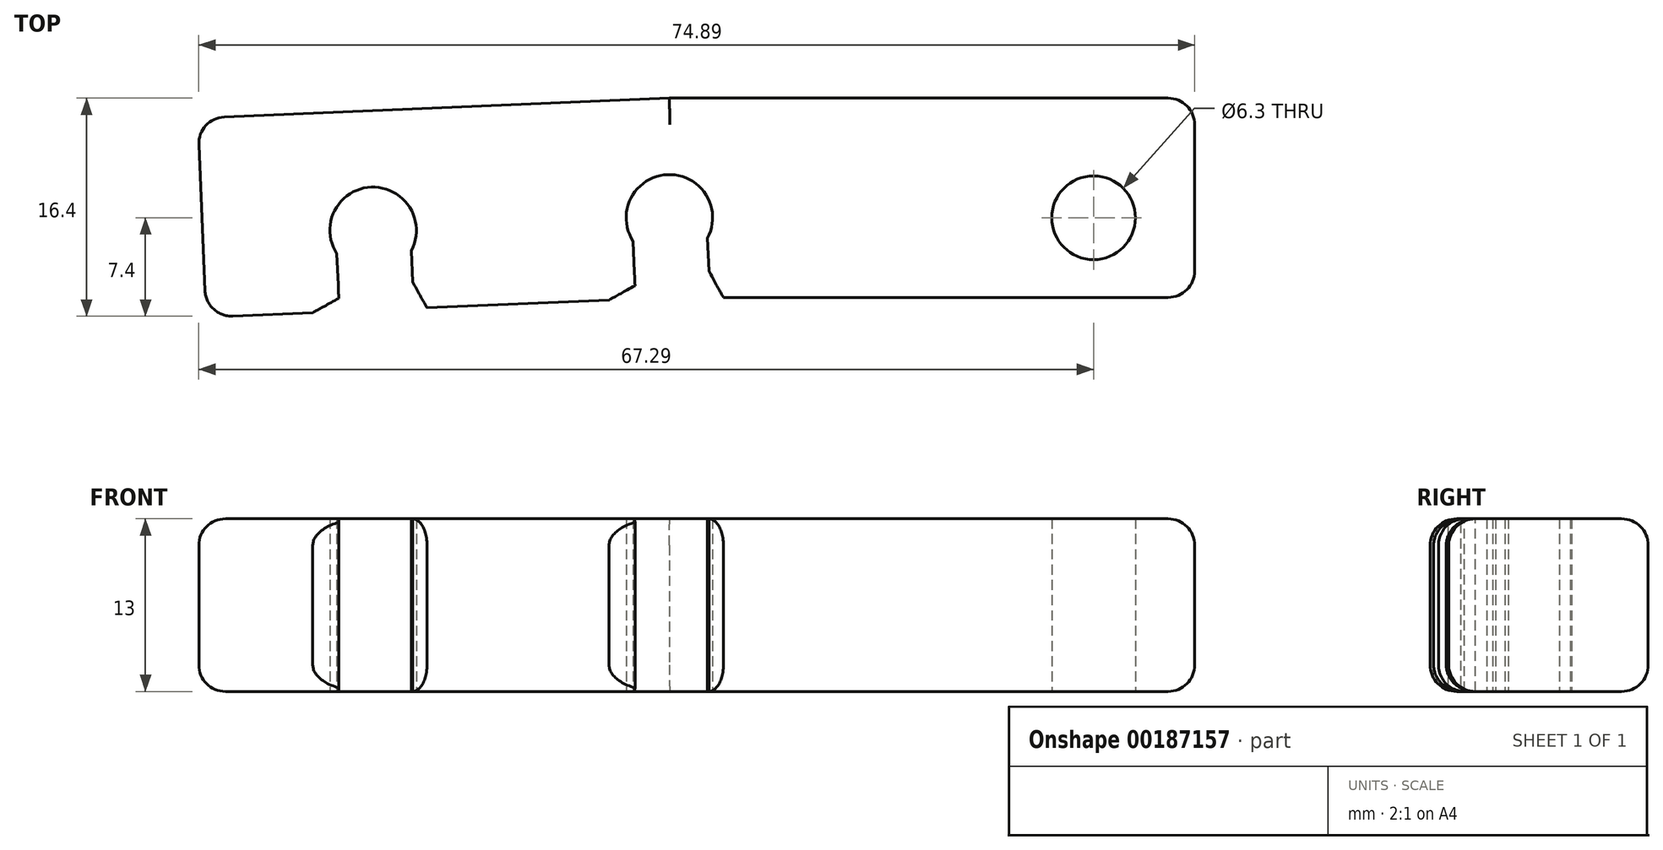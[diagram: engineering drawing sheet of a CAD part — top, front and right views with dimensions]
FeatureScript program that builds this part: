
annotation { "Feature Type Name" : "Feature", "Feature Type Description" : "" }
export const myFeature = defineFeature(function(context is Context, id is Id, definition is map)
    precondition{}
    {
        {
            var Q0;
            Q0=qCreatedBy(makeId("Top.planeOp"),FACE);
            var sketch = newSketch(context, id + "F0", { "sketchPlane" : qUnion([Q0])});
            skCircle(sketch, "E0", {"center": v(0, 0) * mm, "radius": 3.25 * mm});
            skLineSegment(sketch, "E1.bottom", {"start": v(0, 9) * mm, "end": v(39.5, 9) * mm});
            skLineSegment(sketch, "E1.top", {"start": v(0, -6) * mm, "end": v(39.5, -6) * mm});
            skLineSegment(sketch, "E1.left", {"start": v(0, 9) * mm, "end": v(0, -6) * mm});
            skLineSegment(sketch, "E1.right", {"start": v(39.5, 9) * mm, "end": v(39.5, -6) * mm});
            skLineSegment(sketch, "E2", {"start": v(0, 9) * mm, "end": v(-35.47, 7.5) * mm});
            skLineSegment(sketch, "E3", {"start": v(-35.47, 7.5) * mm, "end": v(-34.83, -7.49) * mm});
            skLineSegment(sketch, "E4", {"start": v(-34.83, -7.49) * mm, "end": v(0, -6) * mm});
            skLineSegment(sketch, "E5", {"start": v(0, 9) * mm, "end": v(-35.47, 9) * mm, "construction": true});
            skCircle(sketch, "E6", {"center": v(31.9, 0) * mm, "radius": 3.15 * mm});
            skLineSegment(sketch, "E7", {"start": v(0, 0) * mm, "end": v(-35.09, -1.48) * mm, "construction": true});
            skCircle(sketch, "E8", {"center": v(-22.28, -0.94) * mm, "radius": 3.25 * mm});
            skLineSegment(sketch, "E9", {"start": v(-22.28, -0.94) * mm, "end": v(-22.02, -6.94) * mm, "construction": true});
            skLineSegment(sketch, "E10", {"start": v(0, 0) * mm, "end": v(0.26, -6) * mm, "construction": true});
            skLineSegment(sketch, "E11", {"start": v(-25, -2.71) * mm, "end": v(-24.82, -7.06) * mm});
            skLineSegment(sketch, "E12.MirrorCS", {"start": v(-19.41, -2.47) * mm, "end": v(-19.23, -6.82) * mm});
            skLineSegment(sketch, "E13", {"start": v(-2.73, -1.77) * mm, "end": v(-2.54, -6.1) * mm});
            skLineSegment(sketch, "E14.MirrorCS", {"start": v(2.87, -1.53) * mm, "end": v(3.06, -6) * mm});
            skPoint(sketch, "E15.orphan", {"position": v(3.05, -5.87) * mm});
            skSolve(sketch);
        }
        {
            var Q0;
            {var subQ1=sQuery(id+"F0.wireOp",EDGE,"E2");Q0=makeQuery(id+"F0.imprint","IMPRINT",FACE,{"disambiguationData":[TD([[makeQuery(id+"F0.imprint","IMPRINT",EDGE,{"derivedFrom":subQ1}),1.0]])]});}
            var Q1;
            {var subQ1=sQuery(id+"F0.wireOp",EDGE,"E1.bottom");Q1=makeQuery(id+"F0.imprint","IMPRINT",FACE,{"disambiguationData":[TD([[makeQuery(id+"F0.imprint","IMPRINT",EDGE,{"derivedFrom":subQ1}),-1.0]])]});}
            extrude(context, id + "F1", {"entities" : qUnion([Q0, Q1]), "depth" : 13 * mm, "symmetric" : true});
        }
        {
            var Q0;
            Q0=makeQuery(id+"F1.opExtrude","SWEPT_EDGE",EDGE,{"disambiguationData":[OSD([sQuery(id+"F0.wireOp",EDGE,"E4"),sQuery(id+"F0.wireOp",EDGE,"E11")])]});
            var Q1;
            Q1=makeQuery(id+"F1.opExtrude","SWEPT_EDGE",EDGE,{"disambiguationData":[OSD([sQuery(id+"F0.wireOp",EDGE,"E4"),sQuery(id+"F0.wireOp",EDGE,"E13")])]});
            chamfer(context, id + "F2", {"entities" : qUnion([Q0, Q1]), "chamferType" : ChamferType.TWO_OFFSETS, "width1" : 2 * mm, "oppositeDirection" : false, "width2" : 1 * mm, "tangentPropagation" : true});
        }
        {
            var Q0;
            Q0=makeQuery(id+"F1.opExtrude","SWEPT_EDGE",EDGE,{"disambiguationData":[OSD([sQuery(id+"F0.wireOp",EDGE,"E4"),sQuery(id+"F0.wireOp",EDGE,"E12.MirrorCS")])]});
            var Q1;
            Q1=makeQuery(id+"F1.opExtrude","SWEPT_EDGE",EDGE,{"disambiguationData":[OSD([sQuery(id+"F0.wireOp",EDGE,"E1.top"),sQuery(id+"F0.wireOp",EDGE,"E14.MirrorCS")])]});
            chamfer(context, id + "F3", {"entities" : qUnion([Q0, Q1]), "chamferType" : ChamferType.TWO_OFFSETS, "width1" : 1 * mm, "oppositeDirection" : false, "width2" : 2 * mm, "tangentPropagation" : true});
        }
        {
            var Q0;
            Q0=makeQuery(id+"F1.opExtrude","CAP_EDGE",EDGE,{"disambiguationData":[OSD([sQuery(id+"F0.wireOp",EDGE,"E2")])],"isStart":false});
            var Q1;
            Q1=makeQuery(id+"F1.opExtrude","CAP_EDGE",EDGE,{"disambiguationData":[OSD([sQuery(id+"F0.wireOp",EDGE,"E1.bottom")])],"isStart":false});
            var Q2;
            Q2=makeQuery(id+"F1.opExtrude","CAP_EDGE",EDGE,{"disambiguationData":[OSD([sQuery(id+"F0.wireOp",EDGE,"E2")])],"isStart":true});
            var Q3;
            Q3=makeQuery(id+"F1.opExtrude","CAP_EDGE",EDGE,{"disambiguationData":[OSD([sQuery(id+"F0.wireOp",EDGE,"E1.bottom")])],"isStart":true});
            var Q4;
            Q4=makeQuery(id+"F1.opExtrude","SWEPT_EDGE",EDGE,{"disambiguationData":[OSD([sQuery(id+"F0.wireOp",EDGE,"E2"),sQuery(id+"F0.wireOp",EDGE,"E3")])]});
            var Q5;
            Q5=makeQuery(id+"F1.opExtrude","SWEPT_EDGE",EDGE,{"disambiguationData":[OSD([sQuery(id+"F0.wireOp",EDGE,"E1.bottom"),sQuery(id+"F0.wireOp",EDGE,"E1.right")])]});
            var Q6;
            Q6=makeQuery(id+"F1.opExtrude","CAP_EDGE",EDGE,{"disambiguationData":[OSD([sQuery(id+"F0.wireOp",EDGE,"E1.right")])],"isStart":false});
            var Q7;
            Q7=makeQuery(id+"F1.opExtrude","CAP_EDGE",EDGE,{"disambiguationData":[OSD([sQuery(id+"F0.wireOp",EDGE,"E1.right")])],"isStart":true});
            var Q8;
            Q8=makeQuery(id+"F1.opExtrude","CAP_EDGE",EDGE,{"disambiguationData":[OSD([sQuery(id+"F0.wireOp",EDGE,"E3")])],"isStart":true});
            var Q9;
            Q9=makeQuery(id+"F1.opExtrude","CAP_EDGE",EDGE,{"disambiguationData":[OSD([sQuery(id+"F0.wireOp",EDGE,"E3")])],"isStart":false});
            var Q10;
            Q10=makeQuery(id+"F1.opExtrude","SWEPT_EDGE",EDGE,{"disambiguationData":[OSD([sQuery(id+"F0.wireOp",EDGE,"E3"),sQuery(id+"F0.wireOp",EDGE,"E4")])]});
            var Q11;
            {var subQ0=sQuery(id+"F0.wireOp",EDGE,"E4");Q11=makeQuery(id+"F1.opExtrude","CAP_EDGE",EDGE,{"disambiguationData":[OSD([subQ0]),TDD([makeQuery(id+"F0.imprint","IMPRINT",EDGE,{"disambiguationData":[TD([[makeQuery(id+"F0.imprint","INTERSECT",VERTEX,{"derivedFrom":[sQuery(id+"F0.wireOp",EDGE,"E3"),subQ0]}),-1.0]])],"derivedFrom":subQ0})])],"isStart":true});}
            var Q12;
            {var subQ0=sQuery(id+"F0.wireOp",EDGE,"E4");Q12=makeQuery(id+"F1.opExtrude","CAP_EDGE",EDGE,{"disambiguationData":[OSD([subQ0]),TDD([makeQuery(id+"F0.imprint","IMPRINT",EDGE,{"disambiguationData":[TD([[makeQuery(id+"F0.imprint","INTERSECT",VERTEX,{"derivedFrom":[sQuery(id+"F0.wireOp",EDGE,"E3"),subQ0]}),-1.0]])],"derivedFrom":subQ0})])],"isStart":false});}
            var Q13;
            {var subQ0=sQuery(id+"F0.wireOp",EDGE,"E4");Q13=makeQuery(id+"F1.opExtrude","CAP_EDGE",EDGE,{"disambiguationData":[OSD([subQ0]),TDD([makeQuery(id+"F0.imprint","IMPRINT",EDGE,{"disambiguationData":[TD([[makeQuery(id+"F0.imprint","INTERSECT",VERTEX,{"derivedFrom":[subQ0,sQuery(id+"F0.wireOp",EDGE,"E12.MirrorCS")]}),-1.0]])],"derivedFrom":subQ0})])],"isStart":false});}
            var Q14;
            {var subQ0=sQuery(id+"F0.wireOp",EDGE,"E4");Q14=makeQuery(id+"F1.opExtrude","CAP_EDGE",EDGE,{"disambiguationData":[OSD([subQ0]),TDD([makeQuery(id+"F0.imprint","IMPRINT",EDGE,{"disambiguationData":[TD([[makeQuery(id+"F0.imprint","INTERSECT",VERTEX,{"derivedFrom":[subQ0,sQuery(id+"F0.wireOp",EDGE,"E12.MirrorCS")]}),-1.0]])],"derivedFrom":subQ0})])],"isStart":true});}
            var Q15;
            Q15=makeQuery(id+"F1.opExtrude","CAP_EDGE",EDGE,{"disambiguationData":[OSD([sQuery(id+"F0.wireOp",EDGE,"E1.top")])],"isStart":false});
            var Q16;
            Q16=makeQuery(id+"F1.opExtrude","SWEPT_EDGE",EDGE,{"disambiguationData":[OSD([sQuery(id+"F0.wireOp",EDGE,"E1.top"),sQuery(id+"F0.wireOp",EDGE,"E1.right")])]});
            var Q17;
            Q17=makeQuery(id+"F1.opExtrude","CAP_EDGE",EDGE,{"disambiguationData":[OSD([sQuery(id+"F0.wireOp",EDGE,"E1.top")])],"isStart":true});
            fillet(context, id + "F4", {"entities" : qUnion([Q0, Q1, Q2, Q3, Q4, Q5, Q6, Q7, Q8, Q9, Q10, Q11, Q12, Q13, Q14, Q15, Q16, Q17]), "radius" : 2 * mm, "tangentPropagation" : true, "allowEdgeOverflow" : false});
        }
    });
